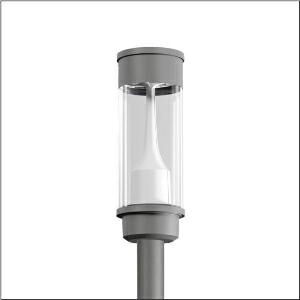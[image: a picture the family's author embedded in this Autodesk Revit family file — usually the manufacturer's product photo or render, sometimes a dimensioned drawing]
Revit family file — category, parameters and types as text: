
# Revit family: litepole_iq___p1_0a_5xa5415ff14h_1a61
name_source: partatom
category: Lighting Fixtures
units: mm (PartAtom-declared; Revit-internal decimal feet)

## family parameters
Cut with Voids When Loaded = No
Host = Face
Light Source = No
Part Type = Normal
Room Calculation Point = No
Round Connector Dimension = Use Diameter
Shared = No

## types (1)
- --- (1 x LED, 1510 lm, 10.5 W, 3000K)
    Apparent Load = 11 VA
    CIE Flux Codes = 32 61 90 93 100
    Color Rendering = 70
    Color Temperature = 3000K
    Default Elevation = 1800 mm
    Description = Litepole iQ, mast luminaire, Module 540 iQ-SR, primary light control with 3 zone facetted reflector, of plastic, silver coated, highly specular, structured, primary optical cover: cover, of PMMA, transparent, light distribution: P1.0a, light emission: direct distribution, primary light characteristic: strongly asymmetric, installation type: post-top, LED, High Power LED, rated luminous flux: 1.510lm, luminous efficacy: 144lm/W, light colour: 730, colour temperature: 3000K, control gear: ECG iQ, control: Auto-Match, Temp-Guard, Lumen-Switch, Night-Set, Smart-Wire, Light-Fading, Desk-Remote (wireless, voltage-free reading and setting of iQ features in the workshop via application-optimized NFC function/RFID function), optimised constant luminous flux control (CLO 2.0), Street-Remote, pre-setting: logarithmic dimming characteristic, with terminal, 6-pole, max. 2.5mm², mains connection: 230..240V, AC, 50/60Hz, start of lifetime: 11W, end of service life: 11W, reduction: 5W, luminaire housing, upper part, of glass-fibre reinforced polyester, coated, Siteco® metallic grey (DB 702S), diameter: 210mm, height: 590mm, spigot size: d x l = 76 x 70mm (post-top) | with reducer (optional accessory) 60 x 70mm, post-top mast mounting element, of diecast aluminium, coated, Siteco® metallic grey (DB 702S), Module 540 iQ-SR, traffic white (RAL 9016), equipment: standard, protection rating (complete): IP65, insulation class (complete): insulation class II (safety insulation), certification: CE, ENEC, VDE, packaging unit: 1 piece

Light Distribution: P1.0a
    Height = 590 mm
    Lamp = 1 x LED
    Lamp Light Flux = 1510 lm
    Lamp Power = 10.5 W
    Lamp count = 1
    Length = 220 mm
    Luminous efficacy = 144 lm/W
    Manufacturer = Siteco
    ModVariant = No
    Model = 5XA5415FF14H
    Number of Poles = 1
    OnlyDefault = Yes
    Power Factor = 1
    Product Name = Litepole iQ | P1.0a
    Product group = mast luminaire | pylon top
    ProductGroupID = 6100
    Protection Class = Protection class II
    Protection Degree = IP 65
    RLX_Detail_Level = 1
    RLX_Emergency_Light_Flux = 0 lm
    RLX_Emergency_Type = 0
    RLX_Emergency_Type_DB = No
    RlxData = <blob elided: 63797 chars, md5=a346bed4>
    Socket = socket
    Standby Power = 0 W
    System Light Flux = 1510 lm
    System Power = 11 W
    Type Comments = factory setting: luminous flux: 100 % | dim-lin: 254 | 419 mA
    Type Image = l_1006025.jpg
    URL = http://relux.com
    VarID = @adj_129087
    Voltage = 0 V
    Weight = 0.00 kg
    Width = 0 mm  [stored 0 ft]

note: [stored X ft] marks values corroborated as IEEE doubles in the binary element streams (Revit-internal decimal feet)

## geometry (parser evidence)
native form markers: Blend x4, Sweep x13
no freeform markers — native parametric forms only
